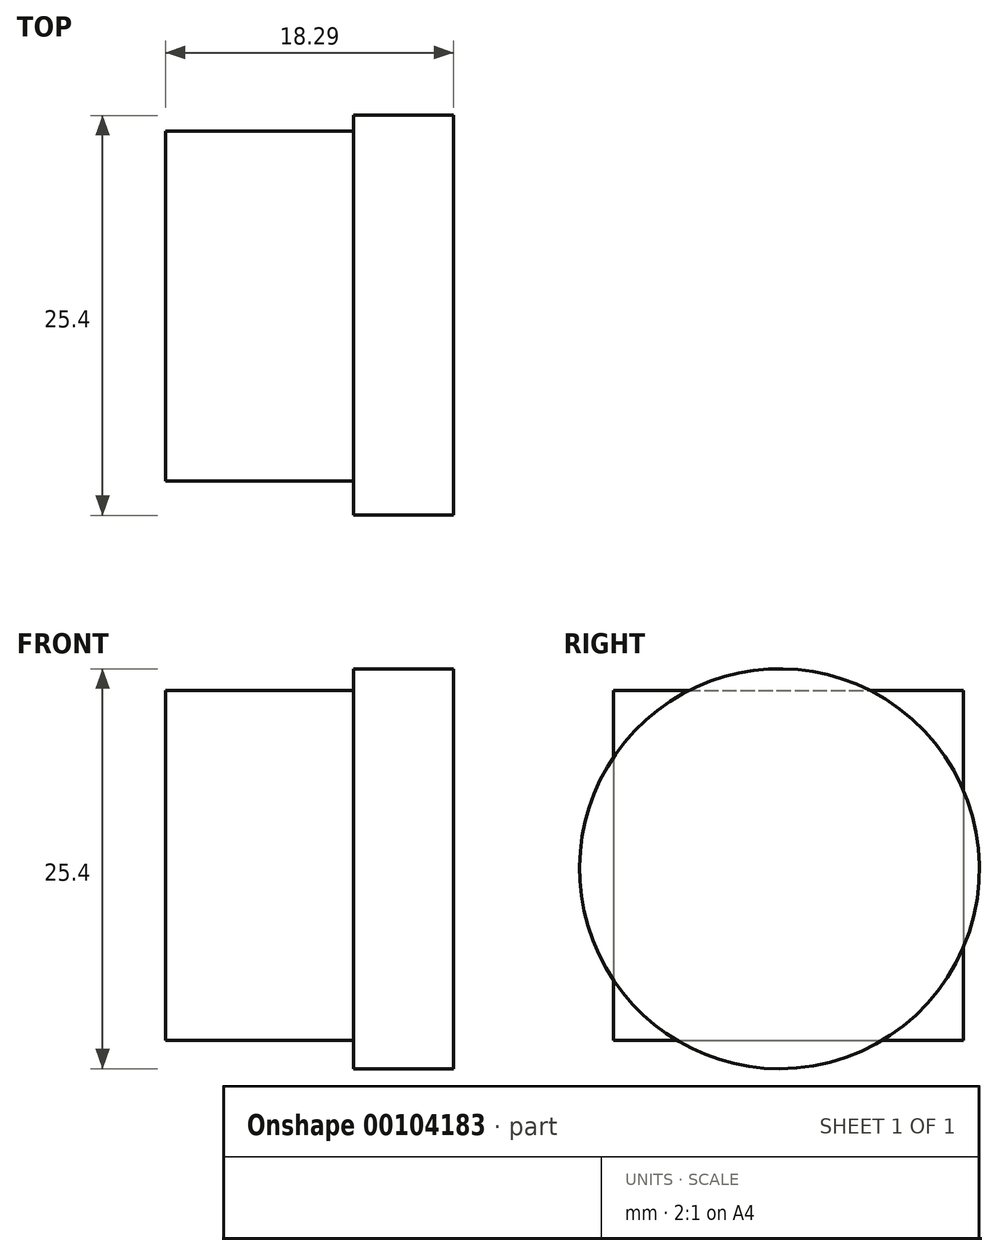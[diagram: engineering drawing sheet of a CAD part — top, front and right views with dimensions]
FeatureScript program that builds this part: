
annotation { "Feature Type Name" : "Feature", "Feature Type Description" : "" }
export const myFeature = defineFeature(function(context is Context, id is Id, definition is map)
    precondition{}
    {
        {
            var Q0;
            Q0=qCreatedBy(makeId("Right.planeOp"),FACE);
            var sketch = newSketch(context, id + "F0", { "sketchPlane" : qUnion([Q0])});
            skLineSegment(sketch, "E0.bottom", {"start": v(-15.3, 37.09) * mm, "end": v(6.93, 37.09) * mm});
            skLineSegment(sketch, "E0.top", {"start": v(-15.3, 14.86) * mm, "end": v(6.93, 14.86) * mm});
            skLineSegment(sketch, "E0.left", {"start": v(-15.3, 37.09) * mm, "end": v(-15.3, 14.86) * mm});
            skLineSegment(sketch, "E0.right", {"start": v(6.93, 37.09) * mm, "end": v(6.93, 14.86) * mm});
            skCircle(sketch, "E1", {"center": v(-4.19, 25.98) * mm, "radius": 5.08 * mm});
            skSolve(sketch);
        }
        {
            var Q0;
            Q0 = qSketchRegion(id + "F0", true);
            extrude(context, id + "F1", {"entities" : qUnion([Q0]), "depth" : 11.94 * mm});
        }
        {
            var Q0;
            Q0=makeQuery(id+"F0.imprint","IMPRINT",FACE,{"disambiguationData":[TD([[makeQuery(id+"F0.imprint","IMPRINT",EDGE,{"derivedFrom":sQuery(id+"F0.wireOp",EDGE,"E1")}),1.0]])]});
            extrude(context, id + "F2", {"entities" : qUnion([Q0]), "operationType" : NewBodyOperationType.ADD, "depth" : 18.29 * mm});
        }
        {
            var Q0;
            Q0=makeQuery(id+"F1.opExtrude","CAP_FACE",FACE,{"disambiguationData":[OSD([sQuery(id+"F0.wireOp",EDGE,"E0.bottom"),sQuery(id+"F0.wireOp",EDGE,"E0.top"),sQuery(id+"F0.wireOp",EDGE,"E0.left"),sQuery(id+"F0.wireOp",EDGE,"E0.right"),sQuery(id+"F0.wireOp",EDGE,"E1")])],"isStart":false});
            cPlane(context, id + "F3", {"entities" : qUnion([Q0]), "cplaneType" : CPlaneType.OFFSET, "offset" : 0 * mm, "width" : 152.4 * mm, "height" : 152.4 * mm});
        }
        {
            var Q0;
            Q0=qCreatedBy(id+"F3.planeOp",FACE);
            var sketch = newSketch(context, id + "F4", { "sketchPlane" : qUnion([Q0])});
            skCircle(sketch, "E2", {"center": v(-4.77, 25.78) * mm, "radius": 12.7 * mm});
            skSolve(sketch);
        }
        {
            var Q0;
            Q0 = qSketchRegion(id + "F4", true);
            extrude(context, id + "F5", {"entities" : qUnion([Q0]), "operationType" : NewBodyOperationType.ADD, "depth" : 6.35 * mm});
        }
    });
